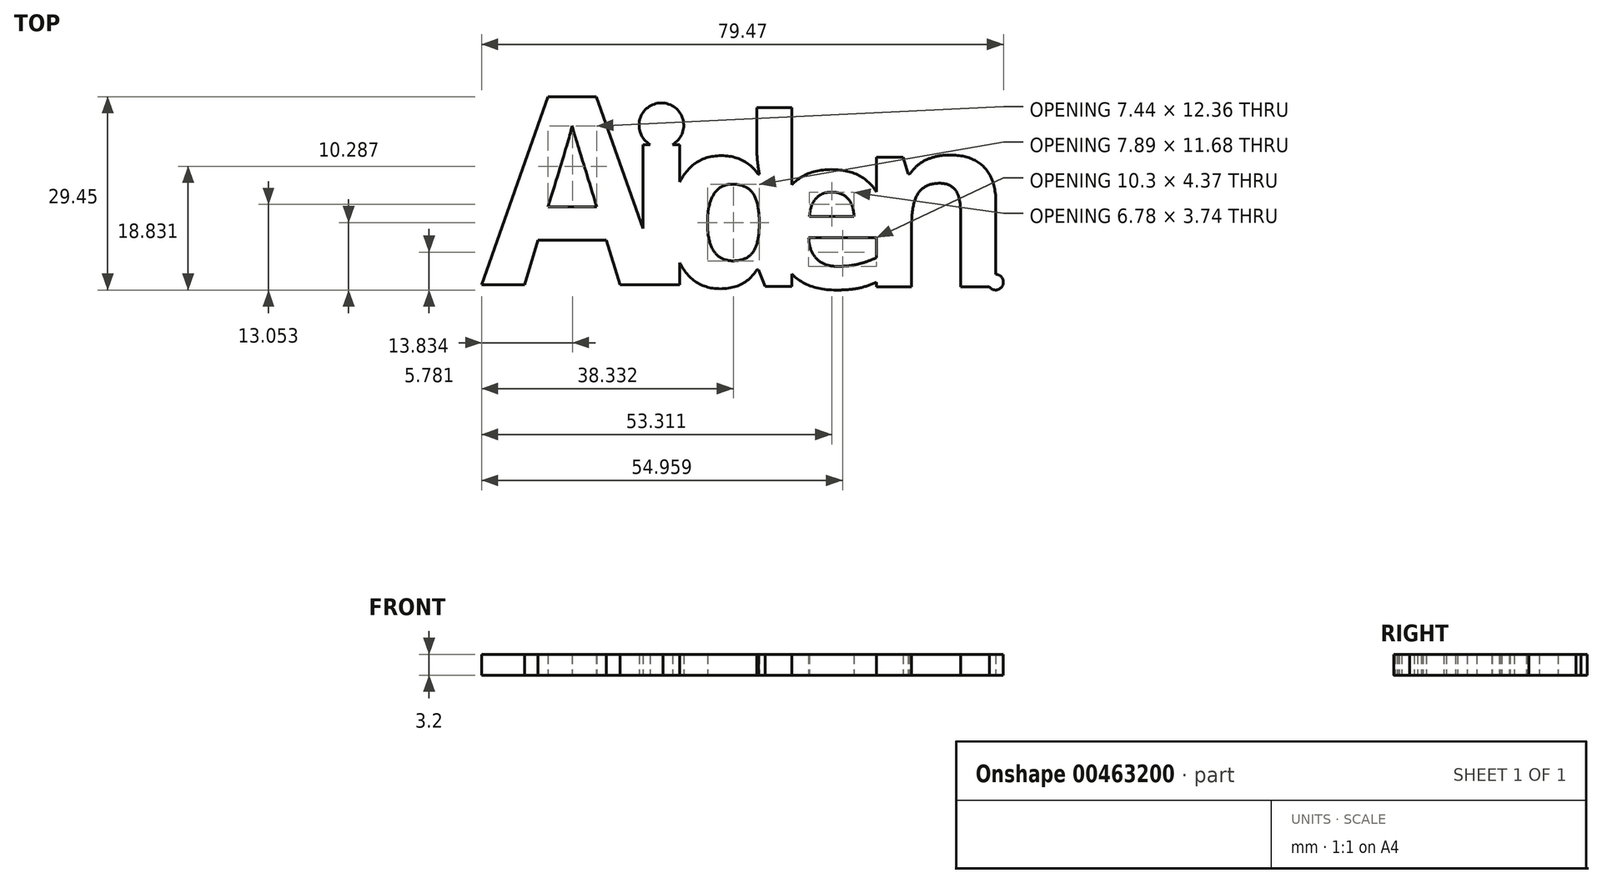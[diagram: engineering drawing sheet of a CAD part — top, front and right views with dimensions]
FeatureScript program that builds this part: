
annotation { "Feature Type Name" : "Feature", "Feature Type Description" : "" }
export const myFeature = defineFeature(function(context is Context, id is Id, definition is map)
    precondition{}
    {
        {
            var Q0;
            Q0=qCreatedBy(makeId("Top.planeOp"),FACE);
            var sketch = newSketch(context, id + "F0", { "sketchPlane" : qUnion([Q0])});
            skText(sketch, "E0", { "text": "A", "fontName": "OpenSans-Bold.ttf"});
            skText(sketch, "E1", { "text": "d", "fontName": "OpenSans-Bold.ttf"});
            skText(sketch, "E2", { "text": "e", "fontName": "OpenSans-Bold.ttf"});
            skText(sketch, "E3", { "text": "n", "fontName": "OpenSans-Bold.ttf"});
            skCircle(sketch, "E4", {"center": v(0, 31.56) * mm, "radius": 4.25 * mm});
            skLineSegment(sketch, "E5.bottom", {"start": v(-3.51, 1.16) * mm, "end": v(3.51, 1.16) * mm});
            skLineSegment(sketch, "E5.top", {"start": v(-3.51, 27.9) * mm, "end": v(3.51, 27.9) * mm});
            skLineSegment(sketch, "E5.left", {"start": v(-3.51, 1.16) * mm, "end": v(-3.51, 27.9) * mm});
            skLineSegment(sketch, "E5.right", {"start": v(3.51, 1.16) * mm, "end": v(3.51, 27.9) * mm});
            skPoint(sketch, "E6", {"position": v(0, 27.9) * mm});
            skArc(sketch, "E7", {"start": v(60.76, 0.78) * mm, "mid": v(66.04, -0.09) * mm, "end": v(63.61, 4.68) * mm});
            skCircle(sketch, "E8", {"center": v(63.62, 1.68) * mm, "radius": 1.5 * mm});
            const initialGuessF0  = {"E0": [-0.03422, 0.00116, 1, 0, 0.03599], "E1": [0, 0.00087, 1, 0, 0.03223], "E2": [0.0201, 0.00058, 1, 0, 0.0292], "E3": [0.03739, 0.00078, 1, 0, 0.03252]};
            skSetInitialGuess(sketch, initialGuessF0);
            skSolve(sketch);
        }
        {
            var Q0;
            Q0 = qSketchRegion(id + "F0", true);
            extrude(context, id + "F1", {"entities" : qUnion([Q0]), "depth" : 4 * mm});
        }
        {
            var Q0;
            Q0=makeQuery(id+"F1.opExtrude","SWEPT_BODY",BODY,{"disambiguationData":[OSD([sQuery(id+"F0.wireOp",EDGE,"E0.sketch_text.stroke-0"),sQuery(id+"F0.wireOp",EDGE,"E0.sketch_text.stroke-1"),sQuery(id+"F0.wireOp",EDGE,"E0.sketch_text.stroke-2"),sQuery(id+"F0.wireOp",EDGE,"E0.sketch_text.stroke-3"),sQuery(id+"F0.wireOp",EDGE,"E0.sketch_text.stroke-4"),sQuery(id+"F0.wireOp",EDGE,"E0.sketch_text.stroke-5"),sQuery(id+"F0.wireOp",EDGE,"E0.sketch_text.stroke-6"),sQuery(id+"F0.wireOp",EDGE,"E0.sketch_text.stroke-7"),sQuery(id+"F0.wireOp",EDGE,"E0.sketch_text.stroke-8"),sQuery(id+"F0.wireOp",EDGE,"E0.sketch_text.stroke-9"),sQuery(id+"F0.wireOp",EDGE,"E0.sketch_text.stroke-10"),sQuery(id+"F0.wireOp",EDGE,"E0.sketch_text.stroke-11"),sQuery(id+"F0.wireOp",EDGE,"E1.sketch_text.stroke-0"),sQuery(id+"F0.wireOp",EDGE,"E1.sketch_text.stroke-1"),sQuery(id+"F0.wireOp",EDGE,"E1.sketch_text.stroke-2"),sQuery(id+"F0.wireOp",EDGE,"E1.sketch_text.stroke-3"),sQuery(id+"F0.wireOp",EDGE,"E1.sketch_text.stroke-4"),sQuery(id+"F0.wireOp",EDGE,"E1.sketch_text.stroke-5"),sQuery(id+"F0.wireOp",EDGE,"E1.sketch_text.stroke-6"),sQuery(id+"F0.wireOp",EDGE,"E1.sketch_text.stroke-7"),sQuery(id+"F0.wireOp",EDGE,"E1.sketch_text.stroke-8"),sQuery(id+"F0.wireOp",EDGE,"E1.sketch_text.stroke-9"),sQuery(id+"F0.wireOp",EDGE,"E1.sketch_text.stroke-10"),sQuery(id+"F0.wireOp",EDGE,"E1.sketch_text.stroke-11"),sQuery(id+"F0.wireOp",EDGE,"E1.sketch_text.stroke-12"),sQuery(id+"F0.wireOp",EDGE,"E1.sketch_text.stroke-13"),sQuery(id+"F0.wireOp",EDGE,"E1.sketch_text.stroke-14"),sQuery(id+"F0.wireOp",EDGE,"E1.sketch_text.stroke-15"),sQuery(id+"F0.wireOp",EDGE,"E1.sketch_text.stroke-16"),sQuery(id+"F0.wireOp",EDGE,"E1.sketch_text.stroke-17"),sQuery(id+"F0.wireOp",EDGE,"E1.sketch_text.stroke-18"),sQuery(id+"F0.wireOp",EDGE,"E1.sketch_text.stroke-19"),sQuery(id+"F0.wireOp",EDGE,"E1.sketch_text.stroke-20"),sQuery(id+"F0.wireOp",EDGE,"E1.sketch_text.stroke-21"),sQuery(id+"F0.wireOp",EDGE,"E1.sketch_text.stroke-22"),sQuery(id+"F0.wireOp",EDGE,"E2.sketch_text.stroke-0"),sQuery(id+"F0.wireOp",EDGE,"E2.sketch_text.stroke-1"),sQuery(id+"F0.wireOp",EDGE,"E2.sketch_text.stroke-2"),sQuery(id+"F0.wireOp",EDGE,"E2.sketch_text.stroke-3"),sQuery(id+"F0.wireOp",EDGE,"E2.sketch_text.stroke-4"),sQuery(id+"F0.wireOp",EDGE,"E2.sketch_text.stroke-5"),sQuery(id+"F0.wireOp",EDGE,"E2.sketch_text.stroke-6"),sQuery(id+"F0.wireOp",EDGE,"E2.sketch_text.stroke-8"),sQuery(id+"F0.wireOp",EDGE,"E2.sketch_text.stroke-9"),sQuery(id+"F0.wireOp",EDGE,"E2.sketch_text.stroke-10"),sQuery(id+"F0.wireOp",EDGE,"E2.sketch_text.stroke-12"),sQuery(id+"F0.wireOp",EDGE,"E2.sketch_text.stroke-13"),sQuery(id+"F0.wireOp",EDGE,"E2.sketch_text.stroke-14"),sQuery(id+"F0.wireOp",EDGE,"E2.sketch_text.stroke-15"),sQuery(id+"F0.wireOp",EDGE,"E2.sketch_text.stroke-16"),sQuery(id+"F0.wireOp",EDGE,"E2.sketch_text.stroke-18"),sQuery(id+"F0.wireOp",EDGE,"E2.sketch_text.stroke-19"),sQuery(id+"F0.wireOp",EDGE,"E3.sketch_text.stroke-0"),sQuery(id+"F0.wireOp",EDGE,"E3.sketch_text.stroke-1"),sQuery(id+"F0.wireOp",EDGE,"E3.sketch_text.stroke-2"),sQuery(id+"F0.wireOp",EDGE,"E3.sketch_text.stroke-3"),sQuery(id+"F0.wireOp",EDGE,"E3.sketch_text.stroke-4"),sQuery(id+"F0.wireOp",EDGE,"E3.sketch_text.stroke-5"),sQuery(id+"F0.wireOp",EDGE,"E3.sketch_text.stroke-6"),sQuery(id+"F0.wireOp",EDGE,"E3.sketch_text.stroke-7"),sQuery(id+"F0.wireOp",EDGE,"E3.sketch_text.stroke-8"),sQuery(id+"F0.wireOp",EDGE,"E3.sketch_text.stroke-9"),sQuery(id+"F0.wireOp",EDGE,"E3.sketch_text.stroke-10"),sQuery(id+"F0.wireOp",EDGE,"E3.sketch_text.stroke-11"),sQuery(id+"F0.wireOp",EDGE,"E3.sketch_text.stroke-12"),sQuery(id+"F0.wireOp",EDGE,"E3.sketch_text.stroke-13"),sQuery(id+"F0.wireOp",EDGE,"E3.sketch_text.stroke-14"),sQuery(id+"F0.wireOp",EDGE,"E3.sketch_text.stroke-15"),sQuery(id+"F0.wireOp",EDGE,"E3.sketch_text.stroke-16"),sQuery(id+"F0.wireOp",EDGE,"E4"),sQuery(id+"F0.wireOp",EDGE,"E5.bottom"),sQuery(id+"F0.wireOp",EDGE,"E5.top"),sQuery(id+"F0.wireOp",EDGE,"E5.left"),sQuery(id+"F0.wireOp",EDGE,"E5.right"),sQuery(id+"F0.wireOp",EDGE,"E7"),sQuery(id+"F0.wireOp",EDGE,"E8")])]});
            var Q1;
            Q1=makeQuery(id+"F1.opExtrude","CAP_VERTEX",VERTEX,{"disambiguationData":[OSD([sQuery(id+"F0.wireOp",EDGE,"E0.sketch_text.stroke-3"),sQuery(id+"F0.wireOp",EDGE,"E0.sketch_text.stroke-4")])],"isStart":true});
            transform(context, id + "F2", {"entities" : qUnion([Q0]), "transformType" : TransformType.SCALE_UNIFORMLY, "scale" : 0.8, "scalePoint" : qUnion([Q1]), "makeCopy" : false});
        }
    });
